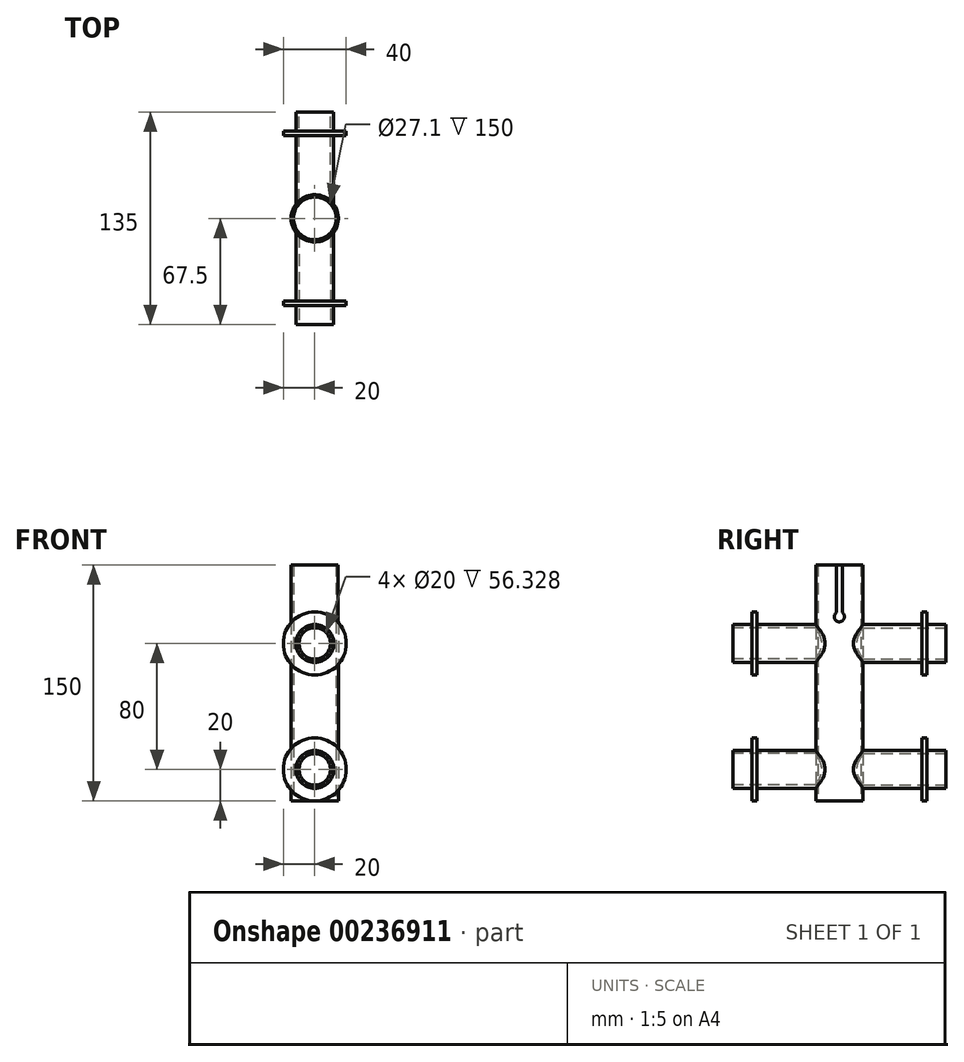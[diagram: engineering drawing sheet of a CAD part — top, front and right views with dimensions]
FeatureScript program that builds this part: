
annotation { "Feature Type Name" : "Feature", "Feature Type Description" : "" }
export const myFeature = defineFeature(function(context is Context, id is Id, definition is map)
    precondition{}
    {
        {
            var Q0;
            Q0=qCreatedBy(makeId("Front.planeOp"),FACE);
            cPlane(context, id + "F0", {"entities" : qUnion([Q0]), "cplaneType" : CPlaneType.OFFSET, "offset" : 135 * mm, "width" : 150 * mm, "height" : 150 * mm});
        }
        {
            var Q0;
            Q0=qCreatedBy(makeId("Front.planeOp"),FACE);
            cPlane(context, id + "F1", {"entities" : qUnion([Q0]), "cplaneType" : CPlaneType.OFFSET, "offset" : 67.5 * mm, "width" : 150 * mm, "height" : 150 * mm});
        }
        {
            var Q0;
            Q0=qCreatedBy(id+"F1.planeOp",FACE);
            var sketch = newSketch(context, id + "F2", { "sketchPlane" : qUnion([Q0])});
            skLineSegment(sketch, "E0", {"start": v(0, 20) * mm, "end": v(0, 0) * mm, "construction": true});
            skLineSegment(sketch, "E1", {"start": v(0, 0) * mm, "end": v(0, -99.27) * mm, "construction": true});
            skLineSegment(sketch, "E2", {"start": v(0, 20) * mm, "end": v(0, 100) * mm, "construction": true});
            skLineSegment(sketch, "E3", {"start": v(0, 100) * mm, "end": v(0, 150) * mm, "construction": true});
            skLineSegment(sketch, "E4", {"start": v(0, 150) * mm, "end": v(15, 150) * mm, "construction": true});
            skLineSegment(sketch, "E5", {"start": v(15, 150) * mm, "end": v(15, 117) * mm, "construction": true});
            skSolve(sketch);
        }
        {
            var Q0;
            Q0=qCreatedBy(makeId("Top.planeOp"),FACE);
            var sketch = newSketch(context, id + "F3", { "sketchPlane" : qUnion([Q0])});
            skLineSegment(sketch, "E6", {"start": v(0, 6.88) * mm, "end": v(0, -67.5) * mm, "construction": true});
            skLineSegment(sketch, "E7", {"start": v(0, -67.5) * mm, "end": v(0, -98.54) * mm, "construction": true});
            skSolve(sketch);
        }
        {
            var Q0;
            Q0=qCreatedBy(makeId("Top.planeOp"),FACE);
            var sketch = newSketch(context, id + "F4", { "sketchPlane" : qUnion([Q0])});
            skCircle(sketch, "E8", {"center": v(0, -67.5) * mm, "radius": 13.55 * mm});
            skCircle(sketch, "E9", {"center": v(0, -67.5) * mm, "radius": 15 * mm});
            skSolve(sketch);
        }
        {
            var Q0;
            Q0=qCreatedBy(id+"F0.planeOp",FACE);
            var sketch = newSketch(context, id + "F5", { "sketchPlane" : qUnion([Q0])});
            skCircle(sketch, "E10", {"center": v(0, 20) * mm, "radius": 10 * mm});
            skCircle(sketch, "E11", {"center": v(0, 20) * mm, "radius": 12 * mm});
            skCircle(sketch, "E12", {"center": v(0, 100) * mm, "radius": 10 * mm});
            skCircle(sketch, "E13", {"center": v(0, 100) * mm, "radius": 12 * mm});
            skCircle(sketch, "E14", {"center": v(0, 20) * mm, "radius": 20 * mm});
            skCircle(sketch, "E15", {"center": v(0, 100) * mm, "radius": 20 * mm});
            skSolve(sketch);
        }
        {
            var Q0;
            Q0=makeQuery(id+"F4.imprint","IMPRINT",FACE,{"disambiguationData":[TD([[makeQuery(id+"F4.imprint","IMPRINT",EDGE,{"derivedFrom":sQuery(id+"F4.wireOp",EDGE,"E8")}),-1.0]])]});
            var Q1;
            Q1=sQuery(id+"F2.wireOp",VERTEX,"E3.end");
            extrude(context, id + "F6", {"entities" : qUnion([Q0]), "endBound" : BoundingType.UP_TO_VERTEX, "endBoundEntityVertex" : qUnion([Q1]), "depth" : 25 * mm});
        }
        {
            var Q0;
            Q0=makeQuery(id+"F5.imprint","IMPRINT",FACE,{"disambiguationData":[TD([[makeQuery(id+"F5.imprint","IMPRINT",EDGE,{"derivedFrom":sQuery(id+"F5.wireOp",EDGE,"E12")}),-1.0]])]});
            var Q1;
            Q1=makeQuery(id+"F5.imprint","IMPRINT",FACE,{"disambiguationData":[TD([[makeQuery(id+"F5.imprint","IMPRINT",EDGE,{"derivedFrom":sQuery(id+"F5.wireOp",EDGE,"E10")}),-1.0]])]});
            var Q2;
            Q2=makeQuery(id+"F6.opExtrude","SWEPT_BODY",BODY,{"disambiguationData":[OSD([sQuery(id+"F4.wireOp",EDGE,"E8"),sQuery(id+"F4.wireOp",EDGE,"E9")])]});
            extrude(context, id + "F7", {"entities" : qUnion([Q0, Q1]), "endBound" : BoundingType.UP_TO_BODY, "oppositeDirection" : true, "endBoundEntityBody" : qUnion([Q2]), "depth" : 25 * mm});
        }
        {
            var Q0;
            Q0=qCreatedBy(makeId("Right.planeOp"),FACE);
            var Q1;
            Q1=sQuery(id+"F2.wireOp",VERTEX,"E5.end");
            cPlane(context, id + "F8", {"entities" : qUnion([Q0, Q1]), "cplaneType" : CPlaneType.PLANE_POINT, "offset" : 25 * mm, "width" : 150 * mm, "height" : 150 * mm});
        }
        {
            var Q0;
            Q0=qCreatedBy(id+"F8.planeOp",FACE);
            var sketch = newSketch(context, id + "F9", { "sketchPlane" : qUnion([Q0])});
            skCircle(sketch, "E16", {"center": v(-67.5, 117) * mm, "radius": 3.25 * mm});
            skLineSegment(sketch, "E17.bottom", {"start": v(-65.5, 117) * mm, "end": v(-69.5, 117) * mm});
            skLineSegment(sketch, "E17.top", {"start": v(-65.5, 150) * mm, "end": v(-69.5, 150) * mm});
            skLineSegment(sketch, "E17.left", {"start": v(-65.5, 117) * mm, "end": v(-65.5, 150) * mm});
            skLineSegment(sketch, "E17.right", {"start": v(-69.5, 117) * mm, "end": v(-69.5, 150) * mm});
            skPoint(sketch, "E17.middle", {"position": v(-67.5, 133.5) * mm});
            skSolve(sketch);
        }
        {
            var Q0;
            {var subQ5=sQuery(id+"F9.wireOp",EDGE,"E17.top");Q0=makeQuery(id+"F9.imprint","IMPRINT",FACE,{"disambiguationData":[TD([[makeQuery(id+"F9.imprint","IMPRINT",EDGE,{"derivedFrom":subQ5}),1.0]])]});}
            var Q1;
            {var subQ5=sQuery(id+"F9.wireOp",EDGE,"E17.bottom");Q1=makeQuery(id+"F9.imprint","IMPRINT",FACE,{"disambiguationData":[TD([[makeQuery(id+"F9.imprint","IMPRINT",EDGE,{"derivedFrom":subQ5}),1.0]])]});}
            var Q2;
            {var subQ5=sQuery(id+"F9.wireOp",EDGE,"E17.bottom");Q2=makeQuery(id+"F9.imprint","IMPRINT",FACE,{"disambiguationData":[TD([[makeQuery(id+"F9.imprint","IMPRINT",EDGE,{"derivedFrom":subQ5}),-1.0]])]});}
            extrude(context, id + "F10", {"entities" : qUnion([Q0, Q1, Q2]), "operationType" : NewBodyOperationType.REMOVE, "oppositeDirection" : true, "depth" : 4 * mm});
        }
        {
            var Q0;
            Q0=makeQuery(id+"F5.imprint","IMPRINT",FACE,{"disambiguationData":[TD([[makeQuery(id+"F5.imprint","IMPRINT",EDGE,{"derivedFrom":sQuery(id+"F5.wireOp",EDGE,"E13")}),-1.0]])]});
            var Q1;
            Q1=makeQuery(id+"F5.imprint","IMPRINT",FACE,{"disambiguationData":[TD([[makeQuery(id+"F5.imprint","IMPRINT",EDGE,{"derivedFrom":sQuery(id+"F5.wireOp",EDGE,"E11")}),-1.0]])]});
            extrude(context, id + "F11", {"entities" : qUnion([Q0, Q1]), "oppositeDirection" : true, "depth" : 15 * mm, "hasSecondDirection" : true, "secondDirectionOppositeDirection" : true, "secondDirectionDepth" : 12 * mm});
        }
        {
            var Q0;
            Q0=makeQuery(id+"F7.opExtrude","SWEPT_BODY",BODY,{"disambiguationData":[OSD([sQuery(id+"F5.wireOp",EDGE,"E12"),sQuery(id+"F5.wireOp",EDGE,"E13")])]});
            var Q1;
            Q1=makeQuery(id+"F11.opExtrude","SWEPT_BODY",BODY,{"disambiguationData":[OSD([sQuery(id+"F5.wireOp",EDGE,"E13"),sQuery(id+"F5.wireOp",EDGE,"E15")])]});
            var Q2;
            Q2=makeQuery(id+"F7.opExtrude","SWEPT_BODY",BODY,{"disambiguationData":[OSD([sQuery(id+"F5.wireOp",EDGE,"E10"),sQuery(id+"F5.wireOp",EDGE,"E11")])]});
            var Q3;
            Q3=makeQuery(id+"F11.opExtrude","SWEPT_BODY",BODY,{"disambiguationData":[OSD([sQuery(id+"F5.wireOp",EDGE,"E11"),sQuery(id+"F5.wireOp",EDGE,"E14")])]});
            var Q4;
            Q4=qCreatedBy(id+"F1.planeOp",FACE);
            mirror(context, id + "F12", {"operationType" : NewBodyOperationType.ADD, "entities" : qUnion([Q0, Q1, Q2, Q3]), "mirrorPlane" : qUnion([Q4])});
        }
    });
